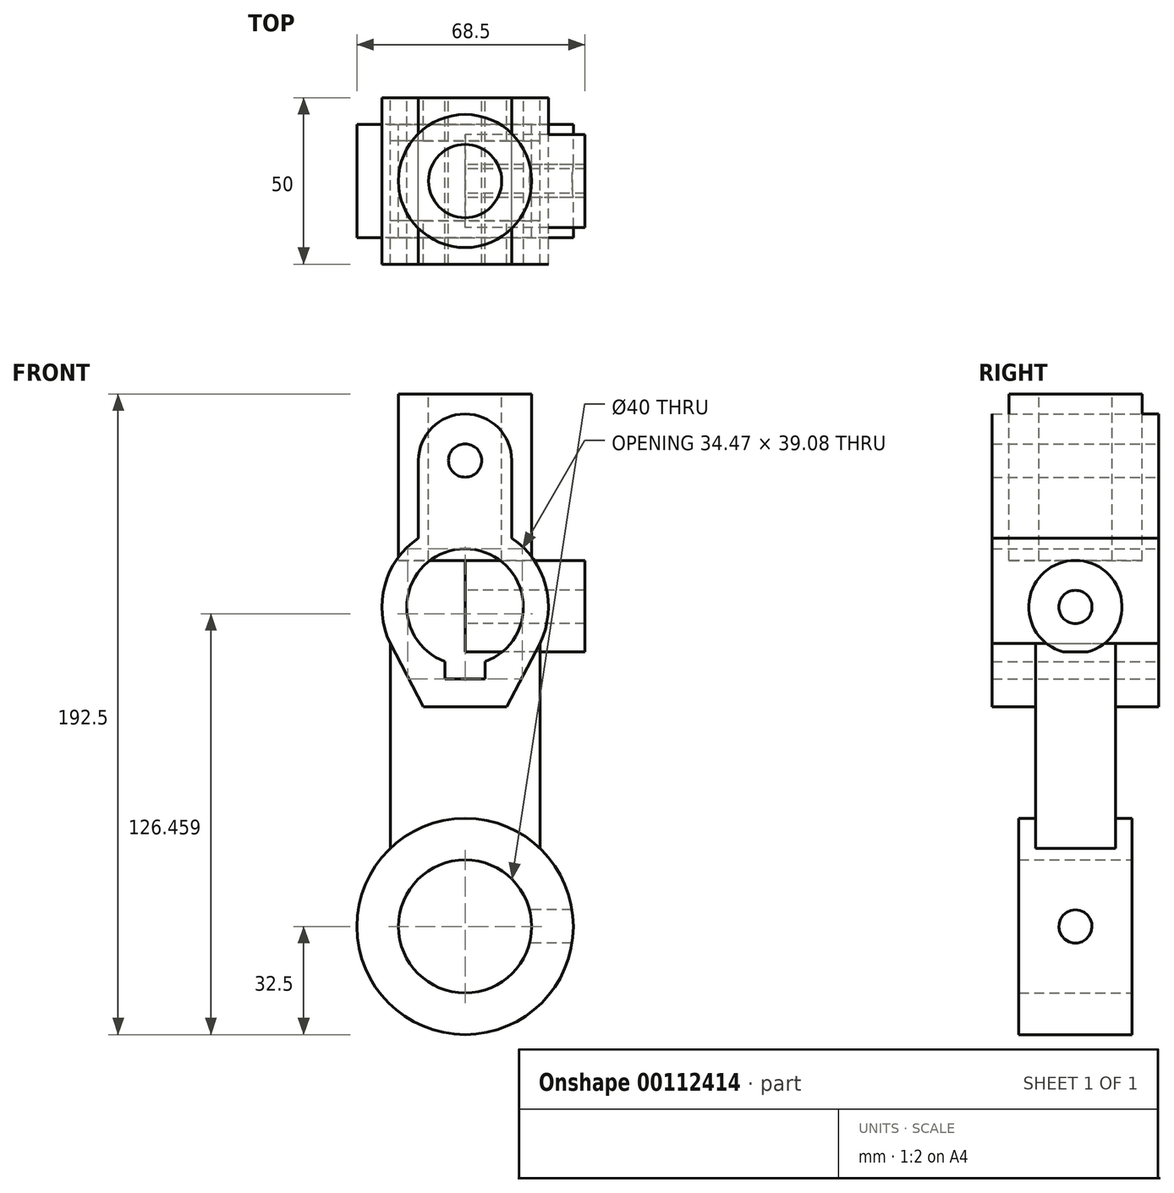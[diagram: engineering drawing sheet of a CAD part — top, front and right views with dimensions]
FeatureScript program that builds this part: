
annotation { "Feature Type Name" : "Feature", "Feature Type Description" : "" }
export const myFeature = defineFeature(function(context is Context, id is Id, definition is map)
    precondition{}
    {
        {
            var Q0;
            Q0=qCreatedBy(makeId("Front.planeOp"),FACE);
            var sketch = newSketch(context, id + "F0", { "sketchPlane" : qUnion([Q0])});
            skCircle(sketch, "E0", {"center": v(0, 0) * mm, "radius": 20 * mm});
            skCircle(sketch, "E1", {"center": v(0, 0) * mm, "radius": 32.5 * mm});
            skLineSegment(sketch, "E2", {"start": v(0, 0) * mm, "end": v(0, 192) * mm, "construction": true});
            skArc(sketch, "E3", {"start": v(6, 79.56) * mm, "mid": v(0, 113.5) * mm, "end": v(-6, 79.56) * mm});
            skCircle(sketch, "E4", {"center": v(0, 140) * mm, "radius": 5 * mm});
            skArc(sketch, "E5", {"start": v(-14, 140) * mm, "mid": v(0, 154) * mm, "end": v(14, 140) * mm});
            skLineSegment(sketch, "E6", {"start": v(-6, 79.56) * mm, "end": v(-6, 74.42) * mm});
            skLineSegment(sketch, "E7.MirrorCS", {"start": v(6, 79.56) * mm, "end": v(6, 74.42) * mm});
            skLineSegment(sketch, "E8", {"start": v(-6, 74.42) * mm, "end": v(6, 74.42) * mm});
            skArc(sketch, "E9", {"start": v(-14, 116.71) * mm, "mid": v(-24.14, 102.5) * mm, "end": v(-22.5, 85.1) * mm});
            skLineSegment(sketch, "E10", {"start": v(0, 66) * mm, "end": v(-12.5, 66) * mm});
            skLineSegment(sketch, "E11.MirrorCS", {"start": v(0, 66) * mm, "end": v(12.5, 66) * mm});
            skLineSegment(sketch, "E12", {"start": v(-12.5, 66) * mm, "end": v(-22.5, 85.1) * mm});
            skLineSegment(sketch, "E13", {"start": v(12.5, 66) * mm, "end": v(22.5, 85.1) * mm});
            skLineSegment(sketch, "E14", {"start": v(-14, 140) * mm, "end": v(-14, 116.71) * mm});
            skLineSegment(sketch, "E15", {"start": v(14, 140) * mm, "end": v(14, 116.71) * mm});
            skArc(sketch, "E16.trimOffspring", {"start": v(22.5, 85.1) * mm, "mid": v(24.14, 102.5) * mm, "end": v(14, 116.71) * mm});
            skLineSegment(sketch, "E17", {"start": v(-22.5, 85.1) * mm, "end": v(-22.5, 23.45) * mm});
            skLineSegment(sketch, "E18.MirrorCS", {"start": v(22.5, 85.1) * mm, "end": v(22.5, 23.45) * mm});
            skSolve(sketch);
        }
        {
            var Q0;
            Q0=qCreatedBy(makeId("Right.planeOp"),FACE);
            var sketch = newSketch(context, id + "F1", { "sketchPlane" : qUnion([Q0])});
            skCircle(sketch, "E19", {"center": v(0, 96) * mm, "radius": 14 * mm});
            skCircle(sketch, "E20", {"center": v(0, 96) * mm, "radius": 5 * mm});
            skCircle(sketch, "E21", {"center": v(0, 0) * mm, "radius": 5 * mm});
            skLineSegment(sketch, "E22.bottom", {"start": v(-12, 82.48) * mm, "end": v(12, 82.48) * mm});
            skLineSegment(sketch, "E22.top", {"start": v(-12, 23.45) * mm, "end": v(12, 23.45) * mm});
            skLineSegment(sketch, "E22.left", {"start": v(-12, 82.48) * mm, "end": v(-12, 23.45) * mm});
            skLineSegment(sketch, "E22.right", {"start": v(12, 82.48) * mm, "end": v(12, 23.45) * mm});
            skSolve(sketch);
        }
        {
            var Q0;
            Q0=qCreatedBy(makeId("Right.planeOp"),FACE);
            var sketch = newSketch(context, id + "F2", { "sketchPlane" : qUnion([Q0])});
            skSolve(sketch);
        }
        {
            var Q0;
            Q0=qCreatedBy(makeId("Top.planeOp"),FACE);
            cPlane(context, id + "F3", {"entities" : qUnion([Q0]), "cplaneType" : CPlaneType.OFFSET, "offset" : 160 * mm, "width" : 150 * mm, "height" : 150 * mm});
        }
        {
            var Q0;
            Q0=qCreatedBy(id+"F3.planeOp",FACE);
            var sketch = newSketch(context, id + "F4", { "sketchPlane" : qUnion([Q0])});
            skCircle(sketch, "E23", {"center": v(0, 0) * mm, "radius": 11 * mm});
            skCircle(sketch, "E24", {"center": v(0, 0) * mm, "radius": 20 * mm});
            skSolve(sketch);
        }
        {
            var Q0;
            Q0 = qSketchRegion(id + "F4", true);
            extrude(context, id + "F5", {"entities" : qUnion([Q0]), "oppositeDirection" : true, "depth" : 50 * mm});
        }
        {
            var Q0;
            Q0=makeQuery(id+"F0.imprint","IMPRINT",FACE,{"disambiguationData":[TD([[makeQuery(id+"F0.imprint","IMPRINT",EDGE,{"derivedFrom":sQuery(id+"F0.wireOp",EDGE,"E3")}),-1.0]])]});
            extrude(context, id + "F6", {"entities" : qUnion([Q0]), "endBound" : BoundingType.SYMMETRIC, "depth" : 50 * mm});
        }
        {
            var Q0;
            Q0=makeQuery(id+"F0.imprint","IMPRINT",FACE,{"disambiguationData":[TD([[makeQuery(id+"F0.imprint","IMPRINT",EDGE,{"derivedFrom":sQuery(id+"F0.wireOp",EDGE,"E0")}),-1.0]])]});
            var Q1;
            Q1 = qSketchRegion(id + "F2", true);
            extrude(context, id + "F7", {"entities" : qUnion([Q0, Q1]), "endBound" : BoundingType.SYMMETRIC, "depth" : 34 * mm});
        }
        {
            var Q0;
            Q0=makeQuery(id+"F1.imprint","IMPRINT",FACE,{"disambiguationData":[TD([[makeQuery(id+"F1.imprint","IMPRINT",EDGE,{"derivedFrom":sQuery(id+"F1.wireOp",EDGE,"E21")}),1.0]])]});
            var Q1;
            Q1=sQuery(id+"F1.wireOp",EDGE,"E21");
            extrude(context, id + "F8", {"entities" : qUnion([Q0]), "operationType" : NewBodyOperationType.REMOVE, "surfaceEntities" : qUnion([Q1]), "depth" : 100 * mm});
        }
        {
            var Q0;
            Q0=makeQuery(id+"F0.imprint","IMPRINT",FACE,{"disambiguationData":[TD([[makeQuery(id+"F0.imprint","IMPRINT",EDGE,{"derivedFrom":sQuery(id+"F0.wireOp",EDGE,"E10")}),1.0]])]});
            extrude(context, id + "F9", {"entities" : qUnion([Q0]), "operationType" : NewBodyOperationType.ADD, "endBound" : BoundingType.SYMMETRIC, "depth" : 24 * mm});
        }
        {
            var Q0;
            Q0=makeQuery(id+"F1.imprint","IMPRINT",FACE,{"disambiguationData":[TD([[makeQuery(id+"F1.imprint","IMPRINT",EDGE,{"derivedFrom":sQuery(id+"F1.wireOp",EDGE,"E20")}),-1.0]])]});
            var Q1;
            Q1=sQuery(id+"F1.wireOp",EDGE,"E19");
            var Q2;
            Q2=sQuery(id+"F1.wireOp",EDGE,"E20");
            extrude(context, id + "F10", {"entities" : qUnion([Q0]), "surfaceEntities" : qUnion([Q1, Q2]), "depth" : 36 * mm});
        }
    });
